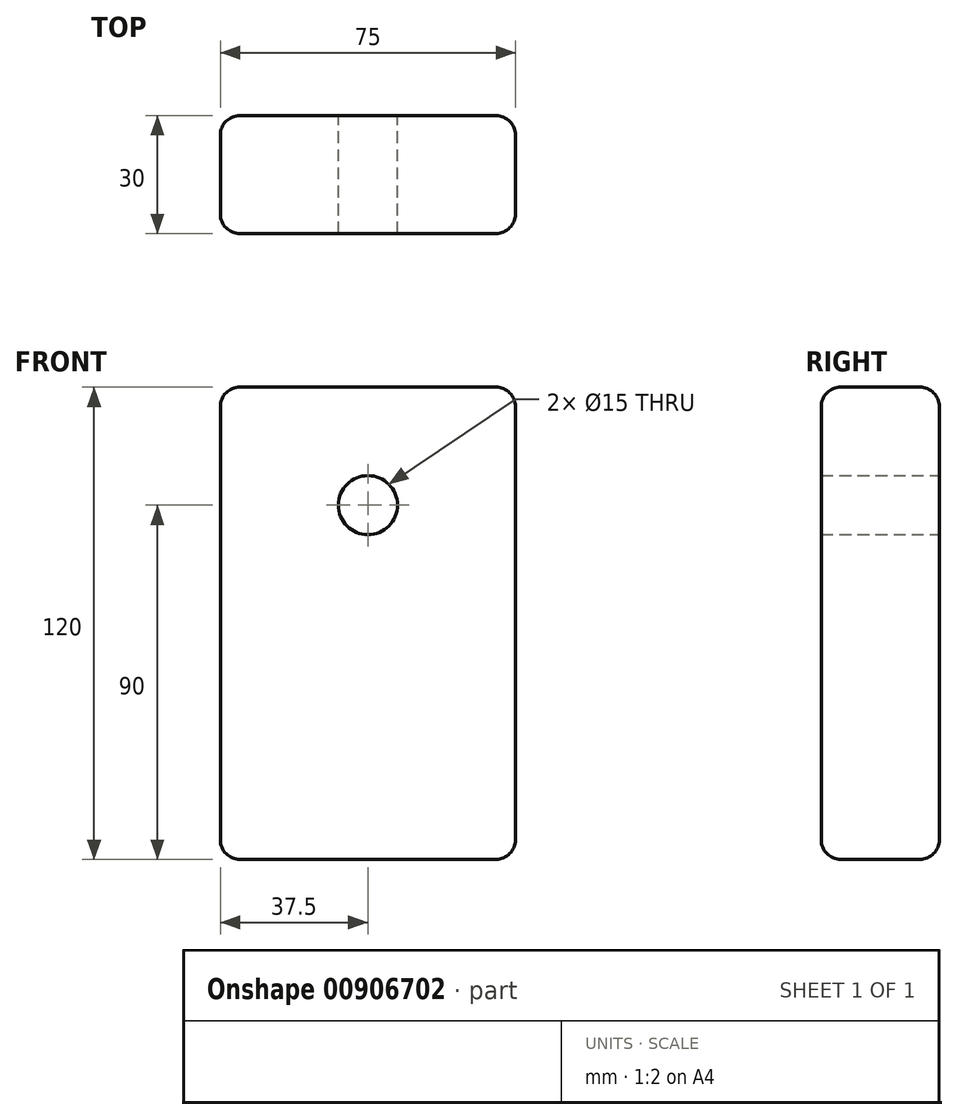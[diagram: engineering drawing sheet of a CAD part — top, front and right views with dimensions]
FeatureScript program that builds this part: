
annotation { "Feature Type Name" : "Feature", "Feature Type Description" : "" }
export const myFeature = defineFeature(function(context is Context, id is Id, definition is map)
    precondition{}
    {
        {
            var Q0;
            Q0=qCreatedBy(makeId("Front.planeOp"),FACE);
            var sketch = newSketch(context, id + "F0", { "sketchPlane" : qUnion([Q0])});
            skLineSegment(sketch, "E0.bottom", {"start": v(0, 0) * mm, "end": v(75, 0) * mm});
            skLineSegment(sketch, "E0.top", {"start": v(0, 120) * mm, "end": v(75, 120) * mm});
            skLineSegment(sketch, "E0.left", {"start": v(0, 0) * mm, "end": v(0, 120) * mm});
            skLineSegment(sketch, "E0.right", {"start": v(75, 0) * mm, "end": v(75, 120) * mm});
            skCircle(sketch, "E1", {"center": v(37.5, 90) * mm, "radius": 7.5 * mm});
            skPoint(sketch, "E1.centerSnap0", {"position": v(37.5, 120) * mm});
            skSolve(sketch);
        }
        {
            var Q0;
            Q0=makeQuery(id+"F0.imprint","IMPRINT",FACE,{"disambiguationData":[TD([[makeQuery(id+"F0.imprint","IMPRINT",EDGE,{"derivedFrom":sQuery(id+"F0.wireOp",EDGE,"E0.bottom")}),1.0]])]});
            extrude(context, id + "F1", {"entities" : qUnion([Q0]), "depth" : 30 * mm, "offsetDistance" : 25 * mm});
        }
        {
            var Q0;
            Q0=makeQuery(id+"F1.opExtrude","CAP_EDGE",EDGE,{"disambiguationData":[OSD([sQuery(id+"F0.wireOp",EDGE,"E0.top")])],"isStart":false});
            var Q1;
            Q1=makeQuery(id+"F1.opExtrude","SWEPT_EDGE",EDGE,{"disambiguationData":[OSD([sQuery(id+"F0.wireOp",EDGE,"E0.top"),sQuery(id+"F0.wireOp",EDGE,"E0.right")])]});
            var Q2;
            Q2=makeQuery(id+"F1.opExtrude","CAP_EDGE",EDGE,{"disambiguationData":[OSD([sQuery(id+"F0.wireOp",EDGE,"E0.top")])],"isStart":true});
            var Q3;
            Q3=makeQuery(id+"F1.opExtrude","SWEPT_EDGE",EDGE,{"disambiguationData":[OSD([sQuery(id+"F0.wireOp",EDGE,"E0.top"),sQuery(id+"F0.wireOp",EDGE,"E0.left")])]});
            var Q4;
            Q4=makeQuery(id+"F1.opExtrude","CAP_EDGE",EDGE,{"disambiguationData":[OSD([sQuery(id+"F0.wireOp",EDGE,"E0.left")])],"isStart":true});
            var Q5;
            Q5=makeQuery(id+"F1.opExtrude","CAP_EDGE",EDGE,{"disambiguationData":[OSD([sQuery(id+"F0.wireOp",EDGE,"E0.left")])],"isStart":false});
            var Q6;
            Q6=makeQuery(id+"F1.opExtrude","CAP_EDGE",EDGE,{"disambiguationData":[OSD([sQuery(id+"F0.wireOp",EDGE,"E0.right")])],"isStart":true});
            var Q7;
            Q7=makeQuery(id+"F1.opExtrude","CAP_EDGE",EDGE,{"disambiguationData":[OSD([sQuery(id+"F0.wireOp",EDGE,"E0.right")])],"isStart":false});
            var Q8;
            Q8=makeQuery(id+"F1.opExtrude","CAP_EDGE",EDGE,{"disambiguationData":[OSD([sQuery(id+"F0.wireOp",EDGE,"E0.bottom")])],"isStart":false});
            var Q9;
            Q9=makeQuery(id+"F1.opExtrude","SWEPT_EDGE",EDGE,{"disambiguationData":[OSD([sQuery(id+"F0.wireOp",EDGE,"E0.bottom"),sQuery(id+"F0.wireOp",EDGE,"E0.right")])]});
            var Q10;
            Q10=makeQuery(id+"F1.opExtrude","CAP_EDGE",EDGE,{"disambiguationData":[OSD([sQuery(id+"F0.wireOp",EDGE,"E0.bottom")])],"isStart":true});
            var Q11;
            Q11=makeQuery(id+"F1.opExtrude","SWEPT_EDGE",EDGE,{"disambiguationData":[OSD([sQuery(id+"F0.wireOp",EDGE,"E0.bottom"),sQuery(id+"F0.wireOp",EDGE,"E0.left")])]});
            fillet(context, id + "F2", {"entities" : qUnion([Q0, Q1, Q2, Q3, Q4, Q5, Q6, Q7, Q8, Q9, Q10, Q11]), "radius" : 5 * mm, "tangentPropagation" : true, "allowEdgeOverflow" : false});
        }
    });
